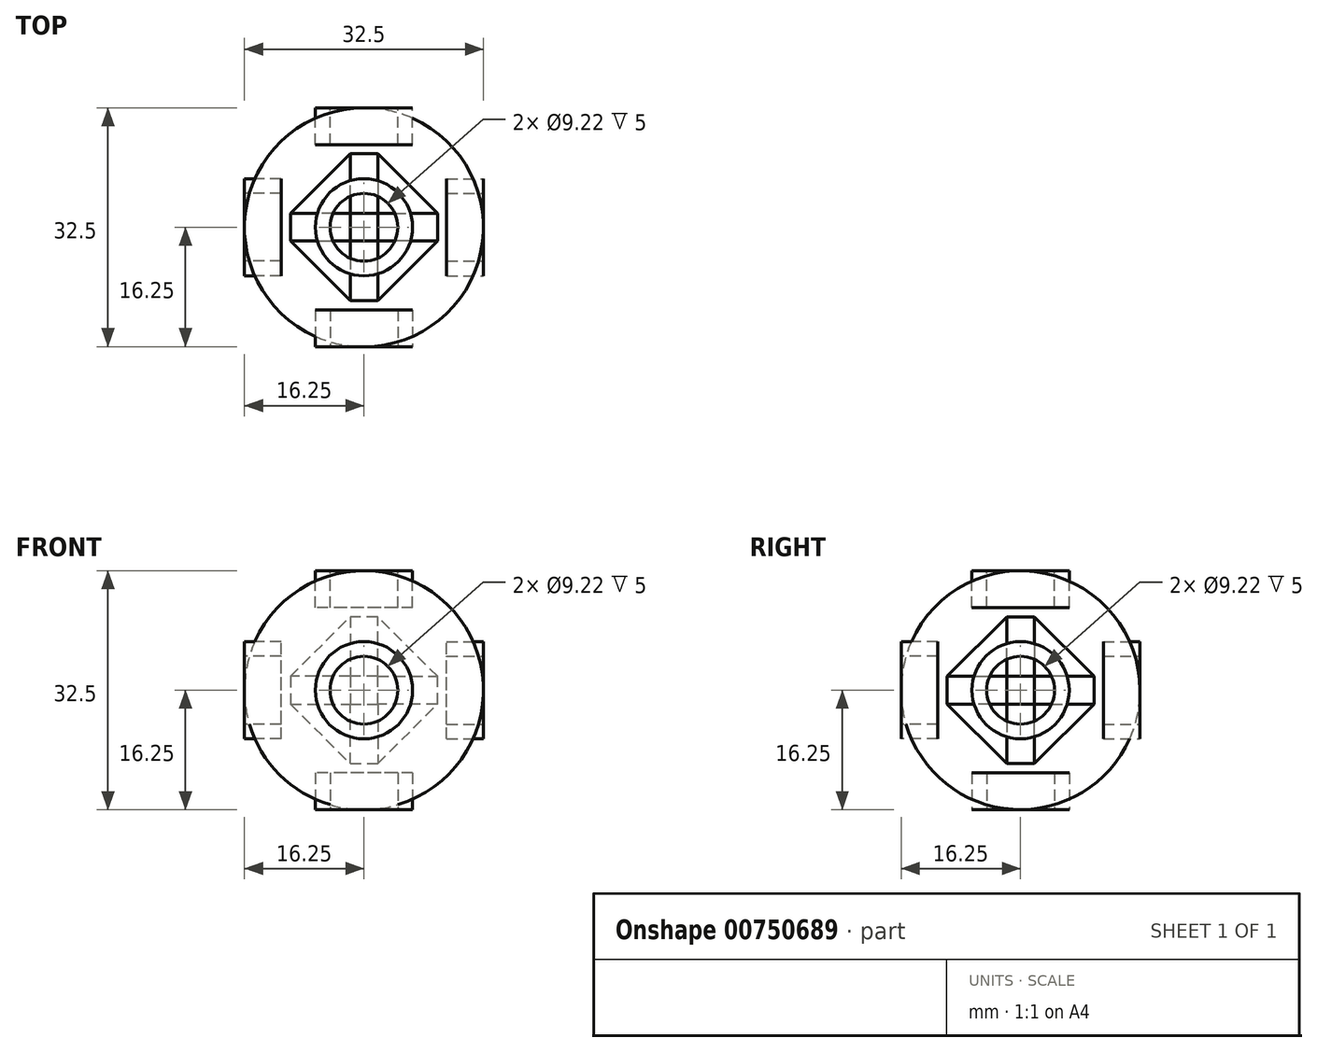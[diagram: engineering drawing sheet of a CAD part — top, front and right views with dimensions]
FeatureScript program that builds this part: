
annotation { "Feature Type Name" : "Feature", "Feature Type Description" : "" }
export const myFeature = defineFeature(function(context is Context, id is Id, definition is map)
    precondition{}
    {
        {
            assignVariable(context, id + "F0", {"name" : "Height", "anyValue" : 32.5});
        }
        {
            var Q0;
            Q0=qCreatedBy(makeId("Front.planeOp"),FACE);
            var sketch = newSketch(context, id + "F1", { "sketchPlane" : qUnion([Q0])});
            skLineSegment(sketch, "E0.bottom", {"start": v(-10, -10) * mm, "end": v(10, -10) * mm});
            skLineSegment(sketch, "E0.top", {"start": v(-10, 10) * mm, "end": v(10, 10) * mm});
            skLineSegment(sketch, "E0.left", {"start": v(-10, -10) * mm, "end": v(-10, 10) * mm});
            skLineSegment(sketch, "E0.right", {"start": v(10, -10) * mm, "end": v(10, 10) * mm});
            skPoint(sketch, "E0.middle", {"position": v(0, 0) * mm});
            skSolve(sketch);
        }
        {
            var Q0;
            Q0=makeQuery(id+"F1.imprint","IMPRINT",FACE,{"disambiguationData":[TD([[makeQuery(id+"F1.imprint","IMPRINT",EDGE,{"derivedFrom":sQuery(id+"F1.wireOp",EDGE,"E0.bottom")}),1.0]])]});
            extrude(context, id + "F2", {"entities" : qUnion([Q0]), "endBound" : BoundingType.SYMMETRIC, "depth" : 20 * mm, "offsetDistance" : 25 * mm});
        }
        {
            var Q0;
            Q0=makeQuery(id+"F2.opExtrude","SWEPT_FACE",FACE,{"disambiguationData":[OSD([sQuery(id+"F1.wireOp",EDGE,"E0.left")])]});
            var Q1;
            Q1=makeQuery(id+"F2.opExtrude","SWEPT_FACE",FACE,{"disambiguationData":[OSD([sQuery(id+"F1.wireOp",EDGE,"E0.right")])]});
            var Q2;
            Q2=makeQuery(id+"F2.opExtrude","SWEPT_FACE",FACE,{"disambiguationData":[OSD([sQuery(id+"F1.wireOp",EDGE,"E0.top")])]});
            var Q3;
            Q3=makeQuery(id+"F2.opExtrude","SWEPT_FACE",FACE,{"disambiguationData":[OSD([sQuery(id+"F1.wireOp",EDGE,"E0.bottom")])]});
            chamfer(context, id + "F3", {"entities" : qUnion([Q0, Q1, Q2, Q3]), "width" : getVariable(context, 'Height') / 4 * mm, "tangentPropagation" : true});
        }
        {
            var Q0;
            Q0=qCreatedBy(makeId("Top.planeOp"),FACE);
            var sketch = newSketch(context, id + "F4", { "sketchPlane" : qUnion([Q0])});
            skCircle(sketch, "E1", {"center": v(0, 0) * mm, "radius": 16.25 * mm});
            skLineSegment(sketch, "E2", {"start": v(0, -16.25) * mm, "end": v(0, 16.25) * mm});
            skSolve(sketch);
        }
        {
            var Q0;
            {var subQ0=sQuery(id+"F4.wireOp",EDGE,"E2");Q0=makeQuery(id+"F4.imprint","IMPRINT",FACE,{"disambiguationData":[TD([[makeQuery(id+"F4.imprint","IMPRINT",EDGE,{"derivedFrom":subQ0}),-1.0]])]});}
            var Q1;
            Q1=sQuery(id+"F4.wireOp",EDGE,"E2");
            revolve(context, id + "F5", {"surfaceOperationType" : NewSurfaceOperationType.NEW, "entities" : qUnion([Q0]), "axis" : qUnion([Q1]), "revolveType" : RevolveType.FULL});
        }
        {
            var Q0;
            Q0=qCreatedBy(makeId("Top.planeOp"),FACE);
            cPlane(context, id + "F6", {"entities" : qUnion([Q0]), "cplaneType" : CPlaneType.OFFSET, "offset" : getVariable(context, 'Height') / 2 * mm, "width" : 150 * mm, "height" : 150 * mm});
        }
        {
            var Q0;
            Q0=qCreatedBy(id+"F6.planeOp",FACE);
            var sketch = newSketch(context, id + "F7", { "sketchPlane" : qUnion([Q0])});
            skCircle(sketch, "E3", {"center": v(0, 0) * mm, "radius": 4.61 * mm});
            skCircle(sketch, "E4", {"center": v(0, 0) * mm, "radius": 6.61 * mm});
            skSolve(sketch);
        }
        {
            var Q0;
            Q0=makeQuery(id+"F7.imprint","IMPRINT",FACE,{"disambiguationData":[TD([[makeQuery(id+"F7.imprint","IMPRINT",EDGE,{"derivedFrom":sQuery(id+"F7.wireOp",EDGE,"E3")}),1.0]])]});
            extrude(context, id + "F8", {"entities" : qUnion([Q0]), "oppositeDirection" : true, "depth" : 10.75 * mm, "offsetDistance" : 25 * mm});
        }
        {
            var Q0;
            Q0=makeQuery(id+"F8.opExtrude","CAP_FACE",FACE,{"disambiguationData":[OSD([sQuery(id+"F7.wireOp",EDGE,"E3")])],"isStart":false});
            chamfer(context, id + "F9", {"entities" : qUnion([Q0]), "chamferType" : ChamferType.OFFSET_ANGLE, "width" : 0.18 * mm, "oppositeDirection" : true, "angle" : 85 * degree, "tangentPropagation" : true});
        }
        {
            var Q0;
            Q0=makeQuery(id+"F7.imprint","IMPRINT",FACE,{"disambiguationData":[TD([[makeQuery(id+"F7.imprint","IMPRINT",EDGE,{"derivedFrom":sQuery(id+"F7.wireOp",EDGE,"E3")}),-1.0]])]});
            extrude(context, id + "F10", {"entities" : qUnion([Q0]), "oppositeDirection" : true, "depth" : 5 * mm, "offsetDistance" : 25 * mm});
        }
        {
            var Q0;
            Q0=makeQuery(id+"F10.opExtrude","SWEPT_BODY",BODY,{"disambiguationData":[OSD([sQuery(id+"F7.wireOp",EDGE,"E3"),sQuery(id+"F7.wireOp",EDGE,"E4")])]});
            var Q1;
            Q1=makeQuery(id+"F8.opExtrude","SWEPT_BODY",BODY,{"disambiguationData":[OSD([sQuery(id+"F7.wireOp",EDGE,"E3")])]});
            var Q2;
            Q2=qCreatedBy(makeId("Top.planeOp"),FACE);
            mirror(context, id + "F11", {"entities" : qUnion([Q0, Q1]), "mirrorPlane" : qUnion([Q2])});
        }
        {
            var Q0;
            Q0=qCreatedBy(makeId("Top.planeOp"),FACE);
            var sketch = newSketch(context, id + "F12", { "sketchPlane" : qUnion([Q0])});
            skLineSegment(sketch, "E5", {"start": v(0, 0) * mm, "end": v(26.37, 0) * mm, "construction": true});
            skLineSegment(sketch, "E6", {"start": v(0, 0) * mm, "end": v(0, 38.93) * mm, "construction": true});
            skSolve(sketch);
        }
        {
            var Q0;
            Q0=qCreatedBy(makeId("Right.planeOp"),FACE);
            var sketch = newSketch(context, id + "F13", { "sketchPlane" : qUnion([Q0])});
            skLineSegment(sketch, "E7", {"start": v(0, 0) * mm, "end": v(0, 47.25) * mm, "construction": true});
            skSolve(sketch);
        }
        {
            var Q0;
            Q0=makeQuery(id+"F11.opPattern","COPY",BODY,{"derivedFrom":makeQuery(id+"F10.opExtrude","SWEPT_BODY",BODY,{"disambiguationData":[OSD([sQuery(id+"F7.wireOp",EDGE,"E3"),sQuery(id+"F7.wireOp",EDGE,"E4")])]}),"instanceName":"1"});
            var Q1;
            Q1=makeQuery(id+"F11.opPattern","COPY",BODY,{"derivedFrom":makeQuery(id+"F8.opExtrude","SWEPT_BODY",BODY,{"disambiguationData":[OSD([sQuery(id+"F7.wireOp",EDGE,"E3")])]}),"instanceName":"1"});
            var Q2;
            Q2=makeQuery(id+"F8.opExtrude","SWEPT_BODY",BODY,{"disambiguationData":[OSD([sQuery(id+"F7.wireOp",EDGE,"E3")])]});
            var Q3;
            Q3=makeQuery(id+"F10.opExtrude","SWEPT_BODY",BODY,{"disambiguationData":[OSD([sQuery(id+"F7.wireOp",EDGE,"E3"),sQuery(id+"F7.wireOp",EDGE,"E4")])]});
            var Q4;
            Q4=sQuery(id+"F12.wireOp",EDGE,"E6");
            transform(context, id + "F14", {"entities" : qUnion([Q0, Q1, Q2, Q3]), "transformType" : TransformType.ROTATION, "transformAxis" : qUnion([Q4]), "angle" : 90 * degree, "makeCopy" : true});
        }
        {
            var Q0;
            Q0=makeQuery(id+"F14.opPattern","COPY",BODY,{"derivedFrom":makeQuery(id+"F11.opPattern","COPY",BODY,{"derivedFrom":makeQuery(id+"F8.opExtrude","SWEPT_BODY",BODY,{"disambiguationData":[OSD([sQuery(id+"F7.wireOp",EDGE,"E3")])]}),"instanceName":"1"}),"instanceName":"1"});
            var Q1;
            Q1=makeQuery(id+"F14.opPattern","COPY",BODY,{"derivedFrom":makeQuery(id+"F11.opPattern","COPY",BODY,{"derivedFrom":makeQuery(id+"F10.opExtrude","SWEPT_BODY",BODY,{"disambiguationData":[OSD([sQuery(id+"F7.wireOp",EDGE,"E3"),sQuery(id+"F7.wireOp",EDGE,"E4")])]}),"instanceName":"1"}),"instanceName":"1"});
            var Q2;
            Q2=makeQuery(id+"F14.opPattern","COPY",BODY,{"derivedFrom":makeQuery(id+"F10.opExtrude","SWEPT_BODY",BODY,{"disambiguationData":[OSD([sQuery(id+"F7.wireOp",EDGE,"E3"),sQuery(id+"F7.wireOp",EDGE,"E4")])]}),"instanceName":"1"});
            var Q3;
            Q3=makeQuery(id+"F14.opPattern","COPY",BODY,{"derivedFrom":makeQuery(id+"F8.opExtrude","SWEPT_BODY",BODY,{"disambiguationData":[OSD([sQuery(id+"F7.wireOp",EDGE,"E3")])]}),"instanceName":"1"});
            var Q4;
            Q4=sQuery(id+"F13.wireOp",EDGE,"E7");
            transform(context, id + "F15", {"entities" : qUnion([Q0, Q1, Q2, Q3]), "transformType" : TransformType.ROTATION, "transformAxis" : qUnion([Q4]), "angle" : 90 * degree, "makeCopy" : true});
        }
        {
            var Q0;
            Q0=makeQuery(id+"F15.opPattern","COPY",BODY,{"derivedFrom":makeQuery(id+"F14.opPattern","COPY",BODY,{"derivedFrom":makeQuery(id+"F8.opExtrude","SWEPT_BODY",BODY,{"disambiguationData":[OSD([sQuery(id+"F7.wireOp",EDGE,"E3")])]}),"instanceName":"1"}),"instanceName":"1"});
            var Q1;
            Q1=makeQuery(id+"F8.opExtrude","SWEPT_BODY",BODY,{"disambiguationData":[OSD([sQuery(id+"F7.wireOp",EDGE,"E3")])]});
            var Q2;
            Q2=makeQuery(id+"F14.opPattern","COPY",BODY,{"derivedFrom":makeQuery(id+"F8.opExtrude","SWEPT_BODY",BODY,{"disambiguationData":[OSD([sQuery(id+"F7.wireOp",EDGE,"E3")])]}),"instanceName":"1"});
            var Q3;
            Q3=makeQuery(id+"F11.opPattern","COPY",BODY,{"derivedFrom":makeQuery(id+"F8.opExtrude","SWEPT_BODY",BODY,{"disambiguationData":[OSD([sQuery(id+"F7.wireOp",EDGE,"E3")])]}),"instanceName":"1"});
            var Q4;
            Q4=makeQuery(id+"F14.opPattern","COPY",BODY,{"derivedFrom":makeQuery(id+"F11.opPattern","COPY",BODY,{"derivedFrom":makeQuery(id+"F8.opExtrude","SWEPT_BODY",BODY,{"disambiguationData":[OSD([sQuery(id+"F7.wireOp",EDGE,"E3")])]}),"instanceName":"1"}),"instanceName":"1"});
            var Q5;
            Q5=makeQuery(id+"F15.opPattern","COPY",BODY,{"derivedFrom":makeQuery(id+"F14.opPattern","COPY",BODY,{"derivedFrom":makeQuery(id+"F11.opPattern","COPY",BODY,{"derivedFrom":makeQuery(id+"F8.opExtrude","SWEPT_BODY",BODY,{"disambiguationData":[OSD([sQuery(id+"F7.wireOp",EDGE,"E3")])]}),"instanceName":"1"}),"instanceName":"1"}),"instanceName":"1"});
            var Q6;
            Q6=makeQuery(id+"F14.opPattern","COPY",BODY,{"derivedFrom":makeQuery(id+"F11.opPattern","COPY",BODY,{"derivedFrom":makeQuery(id+"F10.opExtrude","SWEPT_BODY",BODY,{"disambiguationData":[OSD([sQuery(id+"F7.wireOp",EDGE,"E3"),sQuery(id+"F7.wireOp",EDGE,"E4")])]}),"instanceName":"1"}),"instanceName":"1"});
            booleanBodies(context, id + "F16", {"operationType" : BooleanOperationType.SUBTRACTION, "tools" : qUnion([Q0, Q1, Q2, Q3, Q4, Q5]), "targets" : qUnion([Q6])});
        }
    });
